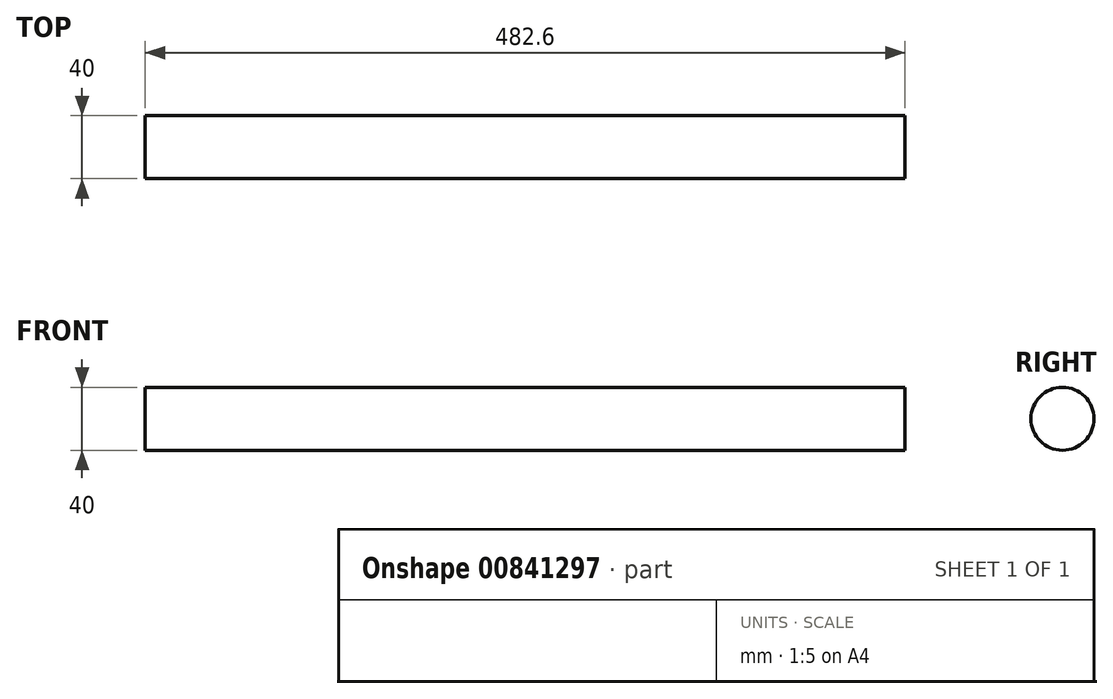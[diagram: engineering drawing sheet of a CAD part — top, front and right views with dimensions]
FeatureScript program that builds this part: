
annotation { "Feature Type Name" : "Feature", "Feature Type Description" : "" }
export const myFeature = defineFeature(function(context is Context, id is Id, definition is map)
    precondition{}
    {
        {
            var Q0;
            Q0=qCreatedBy(makeId("Right.planeOp"),FACE);
            var sketch = newSketch(context, id + "F0", { "sketchPlane" : qUnion([Q0])});
            skCircle(sketch, "E0", {"center": v(0, 0) * mm, "radius": 20 * mm});
            skSolve(sketch);
        }
        {
            var Q0;
            Q0 = qSketchRegion(id + "F0", true);
            extrude(context, id + "F1", {"entities" : qUnion([Q0]), "endBound" : BoundingType.SYMMETRIC, "depth" : 482.6 * mm, "offsetDistance" : 25.4 * mm});
        }
    });
